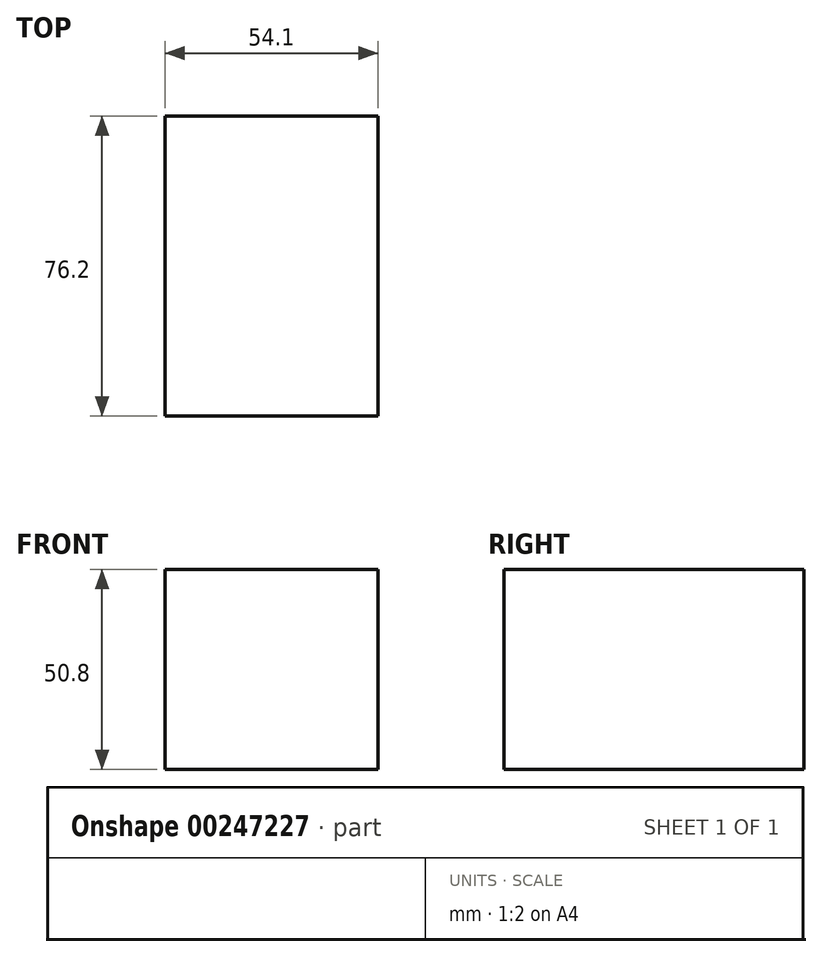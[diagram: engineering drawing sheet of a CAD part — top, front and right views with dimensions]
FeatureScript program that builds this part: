
annotation { "Feature Type Name" : "Feature", "Feature Type Description" : "" }
export const myFeature = defineFeature(function(context is Context, id is Id, definition is map)
    precondition{}
    {
        {
            var Q0;
            Q0=qCreatedBy(makeId("Top.planeOp"),FACE);
            var sketch = newSketch(context, id + "F0", { "sketchPlane" : qUnion([Q0])});
            skLineSegment(sketch, "E0.bottom", {"start": v(0, 0) * mm, "end": v(54.1, 0) * mm});
            skLineSegment(sketch, "E0.top", {"start": v(0, 76.2) * mm, "end": v(54.1, 76.2) * mm});
            skLineSegment(sketch, "E0.left", {"start": v(0, 0) * mm, "end": v(0, 76.2) * mm});
            skLineSegment(sketch, "E0.right", {"start": v(54.1, 0) * mm, "end": v(54.1, 76.2) * mm});
            skSolve(sketch);
        }
        {
            var Q0;
            Q0=makeQuery(id+"F0.imprint","IMPRINT",FACE,{"disambiguationData":[TD([[makeQuery(id+"F0.imprint","IMPRINT",EDGE,{"derivedFrom":sQuery(id+"F0.wireOp",EDGE,"E0.bottom")}),1.0]])]});
            extrude(context, id + "F1", {"entities" : qUnion([Q0]), "depth" : 50.8 * mm});
        }
    });
